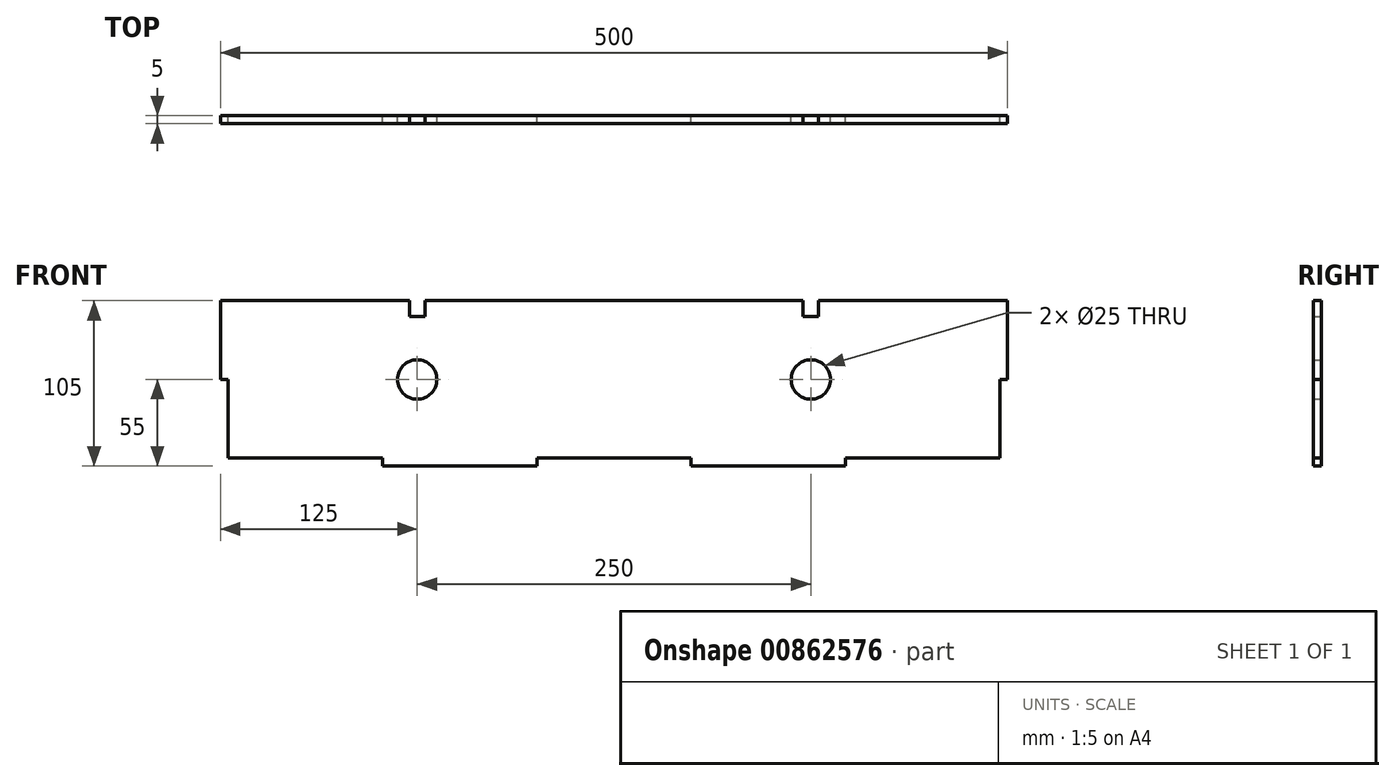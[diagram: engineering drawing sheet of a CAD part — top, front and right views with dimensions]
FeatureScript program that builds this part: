
annotation { "Feature Type Name" : "Feature", "Feature Type Description" : "" }
export const myFeature = defineFeature(function(context is Context, id is Id, definition is map)
    precondition{}
    {
        {
            var Q0;
            Q0=qCreatedBy(makeId("Front.planeOp"),FACE);
            var sketch = newSketch(context, id + "F0", { "sketchPlane" : qUnion([Q0])});
            skLineSegment(sketch, "E0.bottom", {"start": v(245, -50) * mm, "end": v(-245, -50) * mm});
            skLineSegment(sketch, "E0.top", {"start": v(245, 50) * mm, "end": v(130, 50) * mm});
            skLineSegment(sketch, "E0.left", {"start": v(245, -50) * mm, "end": v(245, 50) * mm});
            skLineSegment(sketch, "E0.right", {"start": v(-245, -50) * mm, "end": v(-245, 50) * mm});
            skPoint(sketch, "E0.middle", {"position": v(0, 0) * mm});
            skLineSegment(sketch, "E1", {"start": v(-147, -50) * mm, "end": v(-147, -55) * mm});
            skLineSegment(sketch, "E2", {"start": v(-147, -55) * mm, "end": v(-49, -55) * mm});
            skLineSegment(sketch, "E3", {"start": v(-49, -55) * mm, "end": v(-49, -50) * mm});
            skLineSegment(sketch, "E4", {"start": v(0, 126.03) * mm, "end": v(0, -166.68) * mm});
            skLineSegment(sketch, "E5.MirrorCS", {"start": v(147, -50) * mm, "end": v(147, -55) * mm});
            skLineSegment(sketch, "E6.MirrorCS", {"start": v(147, -55) * mm, "end": v(49, -55) * mm});
            skLineSegment(sketch, "E7.MirrorCS", {"start": v(49, -55) * mm, "end": v(49, -50) * mm});
            skLineSegment(sketch, "E8", {"start": v(-5, 50) * mm, "end": v(-5, -50) * mm});
            skLineSegment(sketch, "E9.MirrorCS", {"start": v(5, 50) * mm, "end": v(5, -50) * mm});
            skLineSegment(sketch, "E10", {"start": v(-245, 50) * mm, "end": v(-5, -50) * mm});
            skLineSegment(sketch, "E11", {"start": v(-245, -50) * mm, "end": v(-5, 50) * mm});
            skCircle(sketch, "E12", {"center": v(-125, 0) * mm, "radius": 12.5 * mm});
            skCircle(sketch, "E13.MirrorC", {"center": v(125, 0) * mm, "radius": 12.5 * mm});
            skLineSegment(sketch, "E14", {"start": v(-245, 50) * mm, "end": v(-250, 50) * mm});
            skLineSegment(sketch, "E15", {"start": v(-250, 50) * mm, "end": v(-250, 0) * mm});
            skLineSegment(sketch, "E16", {"start": v(-250, 0) * mm, "end": v(-245, 0) * mm});
            skLineSegment(sketch, "E17.MirrorCS", {"start": v(245, 50) * mm, "end": v(250, 50) * mm});
            skLineSegment(sketch, "E18.MirrorCS", {"start": v(250, 50) * mm, "end": v(250, 0) * mm});
            skLineSegment(sketch, "E19.MirrorCS", {"start": v(250, 0) * mm, "end": v(245, 0) * mm});
            skLineSegment(sketch, "E20", {"start": v(-125, 40) * mm, "end": v(-130, 40) * mm});
            skLineSegment(sketch, "E21", {"start": v(-130, 40) * mm, "end": v(-130, 50) * mm});
            skLineSegment(sketch, "E22", {"start": v(-125, 0) * mm, "end": v(-125, 82) * mm});
            skLineSegment(sketch, "E23.MirrorCS", {"start": v(-120, 40) * mm, "end": v(-120, 50) * mm});
            skLineSegment(sketch, "E24.MirrorCS", {"start": v(-125, 40) * mm, "end": v(-120, 40) * mm});
            skLineSegment(sketch, "E25.trimOffspring", {"start": v(-130, 50) * mm, "end": v(-245, 50) * mm});
            skLineSegment(sketch, "E26.MirrorCS", {"start": v(130, 40) * mm, "end": v(130, 50) * mm});
            skLineSegment(sketch, "E27.MirrorCS", {"start": v(120, 40) * mm, "end": v(120, 50) * mm});
            skLineSegment(sketch, "E28.MirrorCS", {"start": v(125, 40) * mm, "end": v(120, 40) * mm});
            skLineSegment(sketch, "E29.MirrorCS", {"start": v(125, 40) * mm, "end": v(130, 40) * mm});
            skLineSegment(sketch, "E30.trimOffspring", {"start": v(120, 50) * mm, "end": v(-120, 50) * mm});
            skSolve(sketch);
        }
        {
            var Q0;
            Q0=qSketchRegion(id+"F0",true);
            extrude(context, id + "F1", {"entities" : qUnion([Q0]), "depth" : 5 * mm, "offsetDistance" : 25 * mm});
        }
    });
